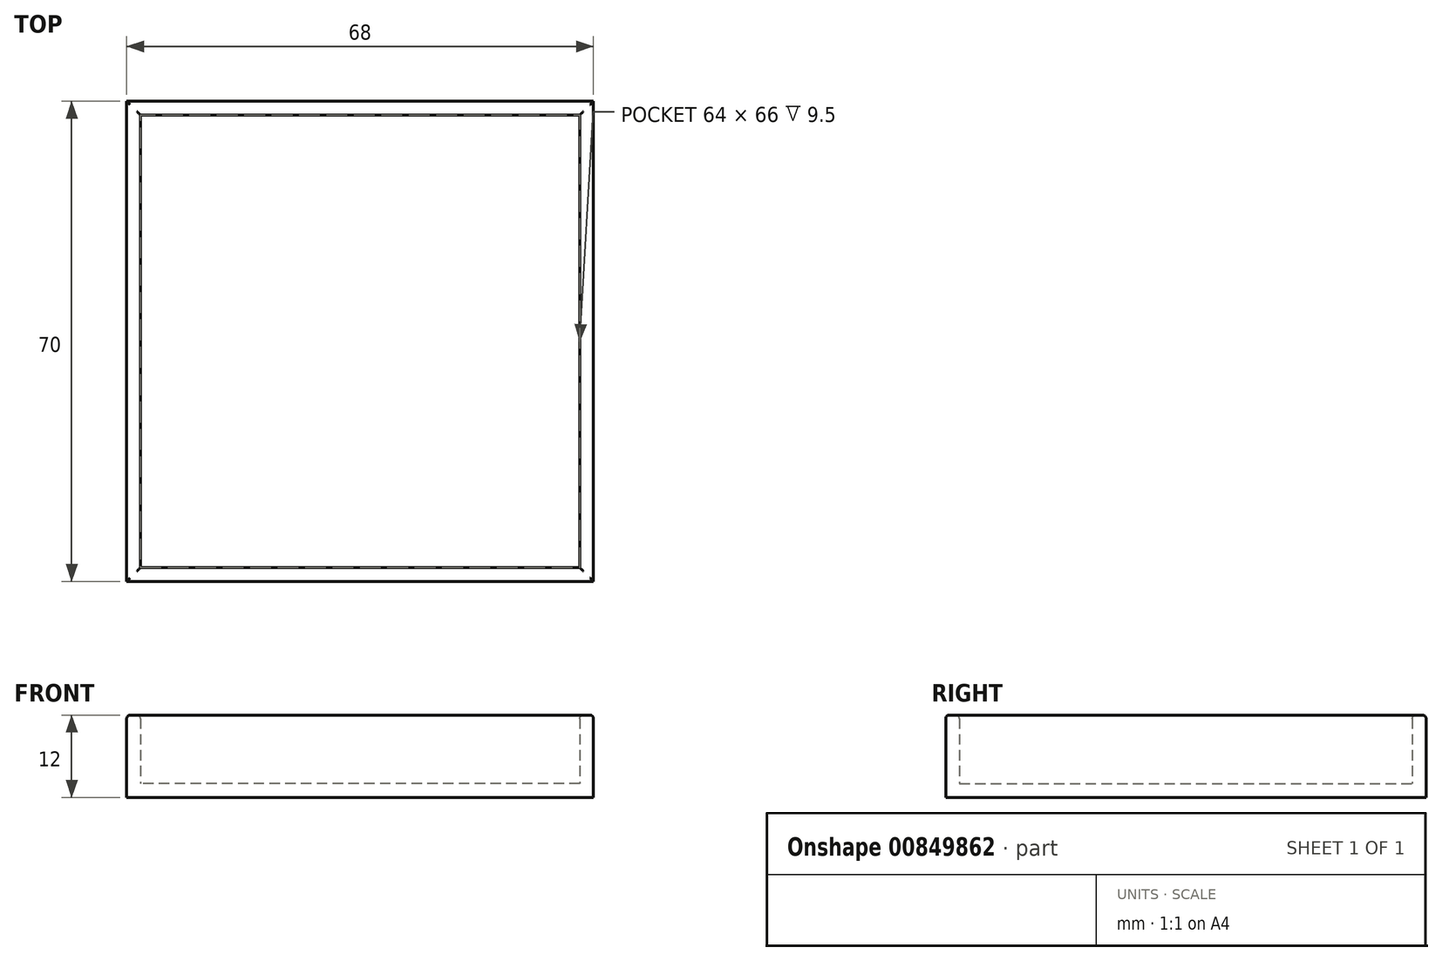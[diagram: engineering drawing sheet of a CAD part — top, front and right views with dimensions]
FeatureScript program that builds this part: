
annotation { "Feature Type Name" : "Feature", "Feature Type Description" : "" }
export const myFeature = defineFeature(function(context is Context, id is Id, definition is map)
    precondition{}
    {
        {
            var Q0;
            Q0=qCreatedBy(makeId("Top.planeOp"),FACE);
            var sketch = newSketch(context, id + "F0", { "sketchPlane" : qUnion([Q0])});
            skLineSegment(sketch, "E0.bottom", {"start": v(-34, 35) * mm, "end": v(34, 35) * mm});
            skLineSegment(sketch, "E0.top", {"start": v(-34, -35) * mm, "end": v(34, -35) * mm});
            skLineSegment(sketch, "E0.left", {"start": v(-34, 35) * mm, "end": v(-34, -35) * mm});
            skLineSegment(sketch, "E0.right", {"start": v(34, 35) * mm, "end": v(34, -35) * mm});
            skPoint(sketch, "E0.middle", {"position": v(0, 0) * mm});
            skLineSegment(sketch, "E1.bottom", {"start": v(-32, 33) * mm, "end": v(32, 33) * mm});
            skLineSegment(sketch, "E1.top", {"start": v(-32, -33) * mm, "end": v(32, -33) * mm});
            skLineSegment(sketch, "E1.left", {"start": v(-32, 33) * mm, "end": v(-32, -33) * mm});
            skLineSegment(sketch, "E1.right", {"start": v(32, 33) * mm, "end": v(32, -33) * mm});
            skSolve(sketch);
        }
        {
            var Q0;
            Q0 = qSketchRegion(id + "F0", true);
            extrude(context, id + "F1", {"entities" : qUnion([Q0]), "depth" : 12 * mm, "offsetDistance" : 25 * mm});
        }
        {
            var Q0;
            Q0=makeQuery(id+"F1.opExtrude","CAP_EDGE",EDGE,{"disambiguationData":[OSD([sQuery(id+"F0.wireOp",EDGE,"E0.left")])],"isStart":false});
            var Q1;
            Q1=makeQuery(id+"F1.opExtrude","CAP_EDGE",EDGE,{"disambiguationData":[OSD([sQuery(id+"F0.wireOp",EDGE,"E0.top")])],"isStart":false});
            var Q2;
            Q2=makeQuery(id+"F1.opExtrude","CAP_EDGE",EDGE,{"disambiguationData":[OSD([sQuery(id+"F0.wireOp",EDGE,"E0.bottom")])],"isStart":false});
            var Q3;
            Q3=makeQuery(id+"F1.opExtrude","CAP_EDGE",EDGE,{"disambiguationData":[OSD([sQuery(id+"F0.wireOp",EDGE,"E0.right")])],"isStart":false});
            var Q4;
            Q4=makeQuery(id+"F1.opExtrude","CAP_EDGE",EDGE,{"disambiguationData":[OSD([sQuery(id+"F0.wireOp",EDGE,"E1.left")])],"isStart":false});
            var Q5;
            Q5=makeQuery(id+"F1.opExtrude","CAP_EDGE",EDGE,{"disambiguationData":[OSD([sQuery(id+"F0.wireOp",EDGE,"E1.bottom")])],"isStart":false});
            var Q6;
            Q6=makeQuery(id+"F1.opExtrude","CAP_EDGE",EDGE,{"disambiguationData":[OSD([sQuery(id+"F0.wireOp",EDGE,"E1.right")])],"isStart":false});
            var Q7;
            Q7=makeQuery(id+"F1.opExtrude","CAP_EDGE",EDGE,{"disambiguationData":[OSD([sQuery(id+"F0.wireOp",EDGE,"E1.top")])],"isStart":false});
            fillet(context, id + "F2", {"entities" : qUnion([Q0, Q1, Q2, Q3, Q4, Q5, Q6, Q7]), "radius" : .5 * mm, "tangentPropagation" : true, "allowEdgeOverflow" : false});
        }
        {
            var Q0;
            Q0=makeQuery(id+"F1.opExtrude","SWEPT_FACE",FACE,{"disambiguationData":[OSD([sQuery(id+"F0.wireOp",EDGE,"E1.bottom")])]});
            var sketch = newSketch(context, id + "F3", { "sketchPlane" : qUnion([Q0])});
            skLineSegment(sketch, "E2.bottom", {"start": v(32, 0) * mm, "end": v(-32, 0) * mm});
            skLineSegment(sketch, "E2.top", {"start": v(32, 2) * mm, "end": v(-32, 2) * mm});
            skLineSegment(sketch, "E2.left", {"start": v(32, 0) * mm, "end": v(32, 2) * mm});
            skLineSegment(sketch, "E2.right", {"start": v(-32, 0) * mm, "end": v(-32, 2) * mm});
            skSolve(sketch);
        }
        {
            var Q0;
            Q0 = qSketchRegion(id + "F3", true);
            extrude(context, id + "F4", {"entities" : qUnion([Q0]), "operationType" : NewBodyOperationType.ADD, "endBound" : BoundingType.UP_TO_NEXT, "depth" : 25 * mm, "offsetDistance" : 25 * mm});
        }
    });
